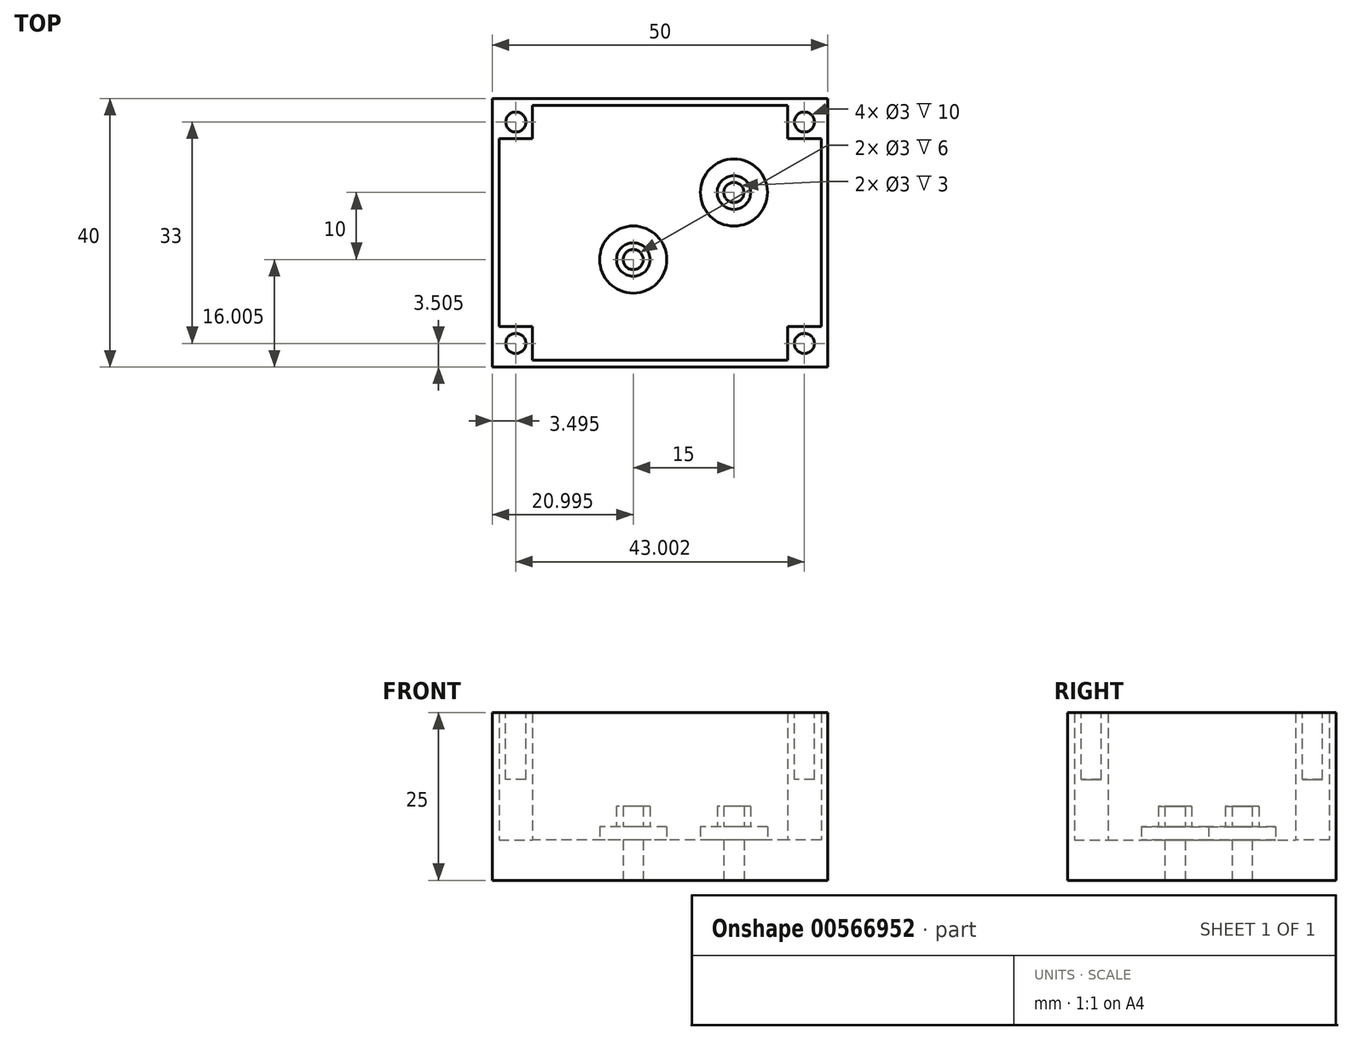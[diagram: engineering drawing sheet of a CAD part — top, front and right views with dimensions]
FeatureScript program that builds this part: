
annotation { "Feature Type Name" : "Feature", "Feature Type Description" : "" }
export const myFeature = defineFeature(function(context is Context, id is Id, definition is map)
    precondition{}
    {
        {
            var Q0;
            Q0=qCreatedBy(makeId("Top.planeOp"),FACE);
            var sketch = newSketch(context, id + "F0", { "sketchPlane" : qUnion([Q0])});
            skLineSegment(sketch, "E0.bottom", {"start": v(-49, 55.2) * mm, "end": v(1, 55.2) * mm});
            skLineSegment(sketch, "E0.top", {"start": v(-49, 15.2) * mm, "end": v(1, 15.2) * mm});
            skLineSegment(sketch, "E0.left", {"start": v(-49, 55.2) * mm, "end": v(-49, 15.2) * mm});
            skLineSegment(sketch, "E0.right", {"start": v(1, 55.2) * mm, "end": v(1, 15.2) * mm});
            skSolve(sketch);
        }
        {
            var Q0;
            Q0=makeQuery(id+"F0.imprint","IMPRINT",FACE,{"disambiguationData":[TD([[makeQuery(id+"F0.imprint","IMPRINT",EDGE,{"derivedFrom":sQuery(id+"F0.wireOp",EDGE,"E0.bottom")}),-1.0]])]});
            extrude(context, id + "F1", {"entities" : qUnion([Q0]), "depth" : 25 * mm, "offsetDistance" : 25 * mm});
        }
        {
            var Q0;
            Q0=makeQuery(id+"F1.opExtrude","CAP_FACE",FACE,{"disambiguationData":[OSD([sQuery(id+"F0.wireOp",EDGE,"E0.bottom"),sQuery(id+"F0.wireOp",EDGE,"E0.top"),sQuery(id+"F0.wireOp",EDGE,"E0.left"),sQuery(id+"F0.wireOp",EDGE,"E0.right")])],"isStart":false});
            var sketch = newSketch(context, id + "F2", { "sketchPlane" : qUnion([Q0])});
            skLineSegment(sketch, "E1.bottom", {"start": v(0, 16.2) * mm, "end": v(-48, 16.2) * mm});
            skLineSegment(sketch, "E1.top", {"start": v(0, 54.2) * mm, "end": v(-48, 54.2) * mm});
            skLineSegment(sketch, "E1.left", {"start": v(0, 16.2) * mm, "end": v(0, 54.2) * mm});
            skLineSegment(sketch, "E1.right", {"start": v(-48, 16.2) * mm, "end": v(-48, 54.2) * mm});
            skPoint(sketch, "E1.middle", {"position": v(-24, 35.2) * mm});
            skPoint(sketch, "E1.middle.positionSnap0", {"position": v(-49, 35.2) * mm});
            skPoint(sketch, "E1.middle.positionSnap1", {"position": v(-24, 55.2) * mm});
            skPoint(sketch, "E1.centerSnap0", {"position": v(-49, 35.2) * mm});
            skPoint(sketch, "E1.centerSnap1", {"position": v(-24, 55.2) * mm});
            skSolve(sketch);
        }
        {
            var Q0;
            Q0=makeQuery(id+"F2.imprint","IMPRINT",FACE,{"disambiguationData":[TD([[makeQuery(id+"F2.imprint","IMPRINT",EDGE,{"derivedFrom":sQuery(id+"F2.wireOp",EDGE,"E1.bottom")}),-1.0]])]});
            extrude(context, id + "F3", {"entities" : qUnion([Q0]), "operationType" : NewBodyOperationType.REMOVE, "oppositeDirection" : true, "depth" : 19 * mm, "offsetDistance" : 25 * mm});
        }
        {
            var Q0;
            Q0=makeQuery(id+"F3.boolean.opBoolean","COPY",FACE,{"derivedFrom":makeQuery(id+"F3.opExtrude","CAP_FACE",FACE,{"disambiguationData":[OSD([sQuery(id+"F2.wireOp",EDGE,"E1.bottom"),sQuery(id+"F2.wireOp",EDGE,"E1.top"),sQuery(id+"F2.wireOp",EDGE,"E1.left"),sQuery(id+"F2.wireOp",EDGE,"E1.right")])],"isStart":false})});
            var sketch = newSketch(context, id + "F4", { "sketchPlane" : qUnion([Q0])});
            skLineSegment(sketch, "E2.bottom", {"start": v(-48, 54.2) * mm, "end": v(-43, 54.2) * mm});
            skLineSegment(sketch, "E2.top", {"start": v(-48, 49.2) * mm, "end": v(-43, 49.2) * mm});
            skLineSegment(sketch, "E2.left", {"start": v(-48, 54.2) * mm, "end": v(-48, 49.2) * mm});
            skLineSegment(sketch, "E2.right", {"start": v(-43, 54.2) * mm, "end": v(-43, 49.2) * mm});
            skLineSegment(sketch, "E3.bottom", {"start": v(-48, 16.2) * mm, "end": v(-43, 16.2) * mm});
            skLineSegment(sketch, "E3.top", {"start": v(-48, 21.2) * mm, "end": v(-43, 21.2) * mm});
            skLineSegment(sketch, "E3.left", {"start": v(-48, 16.2) * mm, "end": v(-48, 21.2) * mm});
            skLineSegment(sketch, "E3.right", {"start": v(-43, 16.2) * mm, "end": v(-43, 21.2) * mm});
            skLineSegment(sketch, "E4.bottom", {"start": v(0, 54.2) * mm, "end": v(-5, 54.2) * mm});
            skLineSegment(sketch, "E4.top", {"start": v(0, 49.2) * mm, "end": v(-5, 49.2) * mm});
            skLineSegment(sketch, "E4.left", {"start": v(0, 54.2) * mm, "end": v(0, 49.2) * mm});
            skLineSegment(sketch, "E4.right", {"start": v(-5, 54.2) * mm, "end": v(-5, 49.2) * mm});
            skLineSegment(sketch, "E5.bottom", {"start": v(0, 16.2) * mm, "end": v(-5, 16.2) * mm});
            skLineSegment(sketch, "E5.top", {"start": v(0, 21.2) * mm, "end": v(-5, 21.2) * mm});
            skLineSegment(sketch, "E5.left", {"start": v(0, 16.2) * mm, "end": v(0, 21.2) * mm});
            skLineSegment(sketch, "E5.right", {"start": v(-5, 16.2) * mm, "end": v(-5, 21.2) * mm});
            skSolve(sketch);
        }
        {
            var Q0;
            Q0 = qSketchRegion(id + "F4", true);
            extrude(context, id + "F5", {"entities" : qUnion([Q0]), "operationType" : NewBodyOperationType.ADD, "depth" : 19 * mm, "offsetDistance" : 25 * mm});
        }
        {
            var Q0;
            Q0=makeQuery(id+"F5.boolean.opBoolean","MERGE",FACE,{"derivedFrom":[makeQuery(id+"F1.opExtrude","CAP_FACE",FACE,{"disambiguationData":[OSD([sQuery(id+"F0.wireOp",EDGE,"E0.bottom"),sQuery(id+"F0.wireOp",EDGE,"E0.top"),sQuery(id+"F0.wireOp",EDGE,"E0.left"),sQuery(id+"F0.wireOp",EDGE,"E0.right")])],"isStart":false}),makeQuery(id+"F5.opExtrude","CAP_FACE",FACE,{"disambiguationData":[OSD([sQuery(id+"F4.wireOp",EDGE,"E2.bottom"),sQuery(id+"F4.wireOp",EDGE,"E2.top"),sQuery(id+"F4.wireOp",EDGE,"E2.left"),sQuery(id+"F4.wireOp",EDGE,"E2.right")])],"isStart":false}),makeQuery(id+"F5.opExtrude","CAP_FACE",FACE,{"disambiguationData":[OSD([sQuery(id+"F4.wireOp",EDGE,"E3.bottom"),sQuery(id+"F4.wireOp",EDGE,"E3.top"),sQuery(id+"F4.wireOp",EDGE,"E3.left"),sQuery(id+"F4.wireOp",EDGE,"E3.right")])],"isStart":false}),makeQuery(id+"F5.opExtrude","CAP_FACE",FACE,{"disambiguationData":[OSD([sQuery(id+"F4.wireOp",EDGE,"E4.bottom"),sQuery(id+"F4.wireOp",EDGE,"E4.top"),sQuery(id+"F4.wireOp",EDGE,"E4.left"),sQuery(id+"F4.wireOp",EDGE,"E4.right")])],"isStart":false}),makeQuery(id+"F5.opExtrude","CAP_FACE",FACE,{"disambiguationData":[OSD([sQuery(id+"F4.wireOp",EDGE,"E5.bottom"),sQuery(id+"F4.wireOp",EDGE,"E5.top"),sQuery(id+"F4.wireOp",EDGE,"E5.left"),sQuery(id+"F4.wireOp",EDGE,"E5.right")])],"isStart":false})]});
            var sketch = newSketch(context, id + "F6", { "sketchPlane" : qUnion([Q0])});
            skCircle(sketch, "E6", {"center": v(-45.5, 51.7) * mm, "radius": 1.5 * mm});
            skPoint(sketch, "E6.centerSnap0", {"position": v(-45.5, 49.2) * mm});
            skPoint(sketch, "E6.centerSnap1", {"position": v(-43, 51.7) * mm});
            skCircle(sketch, "E7", {"center": v(-45.5, 18.7) * mm, "radius": 1.5 * mm});
            skPoint(sketch, "E7.centerSnap0", {"position": v(-45.5, 21.2) * mm});
            skPoint(sketch, "E7.centerSnap1", {"position": v(-43, 18.7) * mm});
            skCircle(sketch, "E8", {"center": v(-2.5, 18.7) * mm, "radius": 1.5 * mm});
            skPoint(sketch, "E8.centerSnap0", {"position": v(-5, 18.7) * mm});
            skPoint(sketch, "E8.centerSnap1", {"position": v(-2.5, 21.2) * mm});
            skCircle(sketch, "E9", {"center": v(-2.5, 51.7) * mm, "radius": 1.5 * mm});
            skPoint(sketch, "E9.centerSnap0", {"position": v(-5, 51.7) * mm});
            skPoint(sketch, "E9.centerSnap1", {"position": v(-2.5, 49.2) * mm});
            skSolve(sketch);
        }
        {
            var Q0;
            Q0 = qSketchRegion(id + "F6", true);
            extrude(context, id + "F7", {"entities" : qUnion([Q0]), "operationType" : NewBodyOperationType.REMOVE, "oppositeDirection" : true, "depth" : 10 * mm, "offsetDistance" : 25 * mm});
        }
        {
            var Q0;
            Q0=makeQuery(id+"F3.boolean.opBoolean","COPY",FACE,{"derivedFrom":makeQuery(id+"F3.opExtrude","CAP_FACE",FACE,{"disambiguationData":[OSD([sQuery(id+"F2.wireOp",EDGE,"E1.bottom"),sQuery(id+"F2.wireOp",EDGE,"E1.top"),sQuery(id+"F2.wireOp",EDGE,"E1.left"),sQuery(id+"F2.wireOp",EDGE,"E1.right")])],"isStart":false})});
            var sketch = newSketch(context, id + "F8", { "sketchPlane" : qUnion([Q0])});
            skCircle(sketch, "E10", {"center": v(-28, 31.2) * mm, "radius": 2.5 * mm});
            skCircle(sketch, "E11", {"center": v(-28, 31.2) * mm, "radius": 1.5 * mm});
            skCircle(sketch, "E12", {"center": v(-13, 41.2) * mm, "radius": 1.5 * mm});
            skCircle(sketch, "E13", {"center": v(-13, 41.2) * mm, "radius": 2.5 * mm});
            skSolve(sketch);
        }
        {
            var Q0;
            Q0 = qSketchRegion(id + "F8", true);
            extrude(context, id + "F9", {"entities" : qUnion([Q0]), "operationType" : NewBodyOperationType.ADD, "depth" : 5 * mm, "offsetDistance" : 25 * mm});
        }
        {
            var Q0;
            Q0=makeQuery(id+"F9.boolean.opBoolean","SPLIT",FACE,{"disambiguationData":[TD([makeQuery(id+"F9.opExtrude","SWEPT_FACE",FACE,{"disambiguationData":[OSD([sQuery(id+"F8.wireOp",EDGE,"E11")])]})])],"derivedFrom":makeQuery(id+"F3.boolean.opBoolean","COPY",FACE,{"derivedFrom":makeQuery(id+"F3.opExtrude","CAP_FACE",FACE,{"disambiguationData":[OSD([sQuery(id+"F2.wireOp",EDGE,"E1.bottom"),sQuery(id+"F2.wireOp",EDGE,"E1.top"),sQuery(id+"F2.wireOp",EDGE,"E1.left"),sQuery(id+"F2.wireOp",EDGE,"E1.right")])],"isStart":false})})});
            var Q1;
            Q1=makeQuery(id+"F9.boolean.opBoolean","SPLIT",FACE,{"disambiguationData":[TD([makeQuery(id+"F9.opExtrude","SWEPT_FACE",FACE,{"disambiguationData":[OSD([sQuery(id+"F8.wireOp",EDGE,"E12")])]})])],"derivedFrom":makeQuery(id+"F3.boolean.opBoolean","COPY",FACE,{"derivedFrom":makeQuery(id+"F3.opExtrude","CAP_FACE",FACE,{"disambiguationData":[OSD([sQuery(id+"F2.wireOp",EDGE,"E1.bottom"),sQuery(id+"F2.wireOp",EDGE,"E1.top"),sQuery(id+"F2.wireOp",EDGE,"E1.left"),sQuery(id+"F2.wireOp",EDGE,"E1.right")])],"isStart":false})})});
            extrude(context, id + "F10", {"entities" : qUnion([Q0, Q1]), "operationType" : NewBodyOperationType.REMOVE, "oppositeDirection" : true, "depth" : 10 * mm, "offsetDistance" : 25 * mm});
        }
        {
            var Q0;
            {var subQ0=sQuery(id+"F2.wireOp",EDGE,"E1.bottom");var subQ1=sQuery(id+"F2.wireOp",EDGE,"E1.top");var subQ2=sQuery(id+"F2.wireOp",EDGE,"E1.left");var subQ3=sQuery(id+"F2.wireOp",EDGE,"E1.right");Q0=makeQuery(id+"F9.boolean.opBoolean","SPLIT",FACE,{"disambiguationData":[TD([makeQuery(id+"F3.boolean.opBoolean","COPY",FACE,{"derivedFrom":makeQuery(id+"F3.opExtrude","SWEPT_FACE",FACE,{"disambiguationData":[OSD([subQ0])]})})])],"derivedFrom":makeQuery(id+"F3.boolean.opBoolean","COPY",FACE,{"derivedFrom":makeQuery(id+"F3.opExtrude","CAP_FACE",FACE,{"disambiguationData":[OSD([subQ0,subQ1,subQ2,subQ3])],"isStart":false})})});}
            var sketch = newSketch(context, id + "F11", { "sketchPlane" : qUnion([Q0])});
            skCircle(sketch, "E14", {"center": v(-28, 31.2) * mm, "radius": 5 * mm});
            skCircle(sketch, "E15", {"center": v(-13, 41.2) * mm, "radius": 5 * mm});
            skSolve(sketch);
        }
        {
            var Q0;
            Q0 = qSketchRegion(id + "F11", true);
            extrude(context, id + "F12", {"entities" : qUnion([Q0]), "operationType" : NewBodyOperationType.ADD, "depth" : 2 * mm, "offsetDistance" : 25 * mm});
        }
        {
            var Q0;
            Q0=makeQuery(id+"F1.opExtrude","CAP_FACE",FACE,{"disambiguationData":[OSD([sQuery(id+"F0.wireOp",EDGE,"E0.bottom"),sQuery(id+"F0.wireOp",EDGE,"E0.top"),sQuery(id+"F0.wireOp",EDGE,"E0.left"),sQuery(id+"F0.wireOp",EDGE,"E0.right")])],"isStart":true});
            var sketch = newSketch(context, id + "F13", { "sketchPlane" : qUnion([Q0])});
            skCircle(sketch, "E16", {"center": v(-28, -31.2) * mm, "radius": 3 * mm});
            skCircle(sketch, "E17", {"center": v(-13, -41.2) * mm, "radius": 3 * mm});
            skCircle(sketch, "E18.cCircle", {"center": v(-28, -31.2) * mm, "radius": 3 * mm, "construction": true});
            skLineSegment(sketch, "E18.0", {"start": v(-26.56, -33.83) * mm, "end": v(-29.55, -33.77) * mm});
            skLineSegment(sketch, "E18.1", {"start": v(-29.55, -33.77) * mm, "end": v(-31, -31.15) * mm});
            skLineSegment(sketch, "E18.2", {"start": v(-31, -31.15) * mm, "end": v(-29.45, -28.58) * mm});
            skLineSegment(sketch, "E18.3", {"start": v(-29.45, -28.58) * mm, "end": v(-26.45, -28.64) * mm});
            skLineSegment(sketch, "E18.4", {"start": v(-26.45, -28.64) * mm, "end": v(-25, -31.26) * mm});
            skLineSegment(sketch, "E18.5", {"start": v(-25, -31.26) * mm, "end": v(-26.56, -33.83) * mm});
            skCircle(sketch, "E19.cCircle", {"center": v(-13, -41.2) * mm, "radius": 3 * mm, "construction": true});
            skLineSegment(sketch, "E19.0", {"start": v(-10.25, -42.4) * mm, "end": v(-12.66, -44.18) * mm});
            skLineSegment(sketch, "E19.1", {"start": v(-12.66, -44.18) * mm, "end": v(-15.41, -43) * mm});
            skLineSegment(sketch, "E19.2", {"start": v(-15.41, -43) * mm, "end": v(-15.76, -40.02) * mm});
            skLineSegment(sketch, "E19.3", {"start": v(-15.76, -40.02) * mm, "end": v(-13.35, -38.22) * mm});
            skLineSegment(sketch, "E19.4", {"start": v(-13.35, -38.22) * mm, "end": v(-10.6, -39.41) * mm});
            skLineSegment(sketch, "E19.5", {"start": v(-10.6, -39.41) * mm, "end": v(-10.25, -42.4) * mm});
            skSolve(sketch);
        }
        {
            var Q0;
            Q0=makeQuery(id+"F13.imprint","IMPRINT",FACE,{"disambiguationData":[TD([[makeQuery(id+"F13.imprint","IMPRINT",EDGE,{"derivedFrom":sQuery(id+"F13.wireOp",EDGE,"E18.0")}),-1.0]])]});
            var Q1;
            Q1=makeQuery(id+"F13.imprint","IMPRINT",FACE,{"disambiguationData":[TD([[makeQuery(id+"F13.imprint","IMPRINT",EDGE,{"derivedFrom":sQuery(id+"F13.wireOp",EDGE,"E19.0")}),-1.0]])]});
            extrude(context, id + "F14", {"entities" : qUnion([Q0, Q1]), "operationType" : NewBodyOperationType.REMOVE, "depth" : 5 * mm, "offsetDistance" : 25 * mm});
        }
    });
